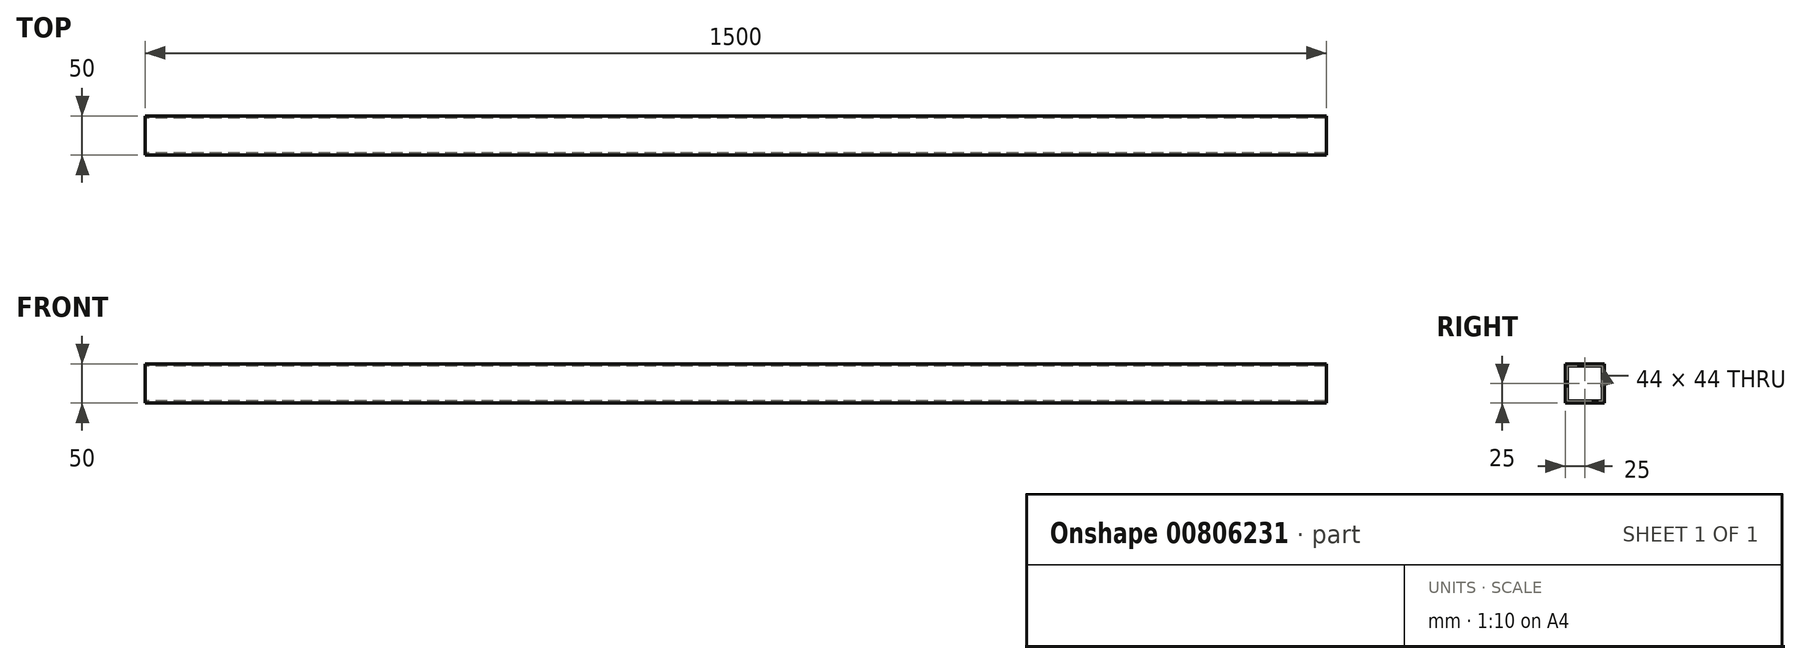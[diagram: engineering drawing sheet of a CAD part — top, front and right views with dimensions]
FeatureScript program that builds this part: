
annotation { "Feature Type Name" : "Feature", "Feature Type Description" : "" }
export const myFeature = defineFeature(function(context is Context, id is Id, definition is map)
    precondition{}
    {
        {
            var Q0;
            Q0=qCreatedBy(makeId("Right.planeOp"),FACE);
            var sketch = newSketch(context, id + "F0", { "sketchPlane" : qUnion([Q0])});
            skLineSegment(sketch, "E0.bottom", {"start": v(25, -25) * mm, "end": v(-25, -25) * mm});
            skLineSegment(sketch, "E0.top", {"start": v(25, 25) * mm, "end": v(-25, 25) * mm});
            skLineSegment(sketch, "E0.left", {"start": v(25, -25) * mm, "end": v(25, 25) * mm});
            skLineSegment(sketch, "E0.right", {"start": v(-25, -25) * mm, "end": v(-25, 25) * mm});
            skPoint(sketch, "E0.middle", {"position": v(0, 0) * mm});
            skLineSegment(sketch, "E1.0", {"start": v(22, 22) * mm, "end": v(-22, 22) * mm});
            skLineSegment(sketch, "E1.1", {"start": v(22, -22) * mm, "end": v(22, 22) * mm});
            skLineSegment(sketch, "E1.2", {"start": v(22, -22) * mm, "end": v(-22, -22) * mm});
            skLineSegment(sketch, "E1.3", {"start": v(-22, -22) * mm, "end": v(-22, 22) * mm});
            skSolve(sketch);
        }
        {
            var Q0;
            Q0=qSketchRegion(id+"F0",true);
            extrude(context, id + "F1", {"entities" : qUnion([Q0]), "depth" : 1500 * mm, "offsetDistance" : 25 * mm});
        }
    });
